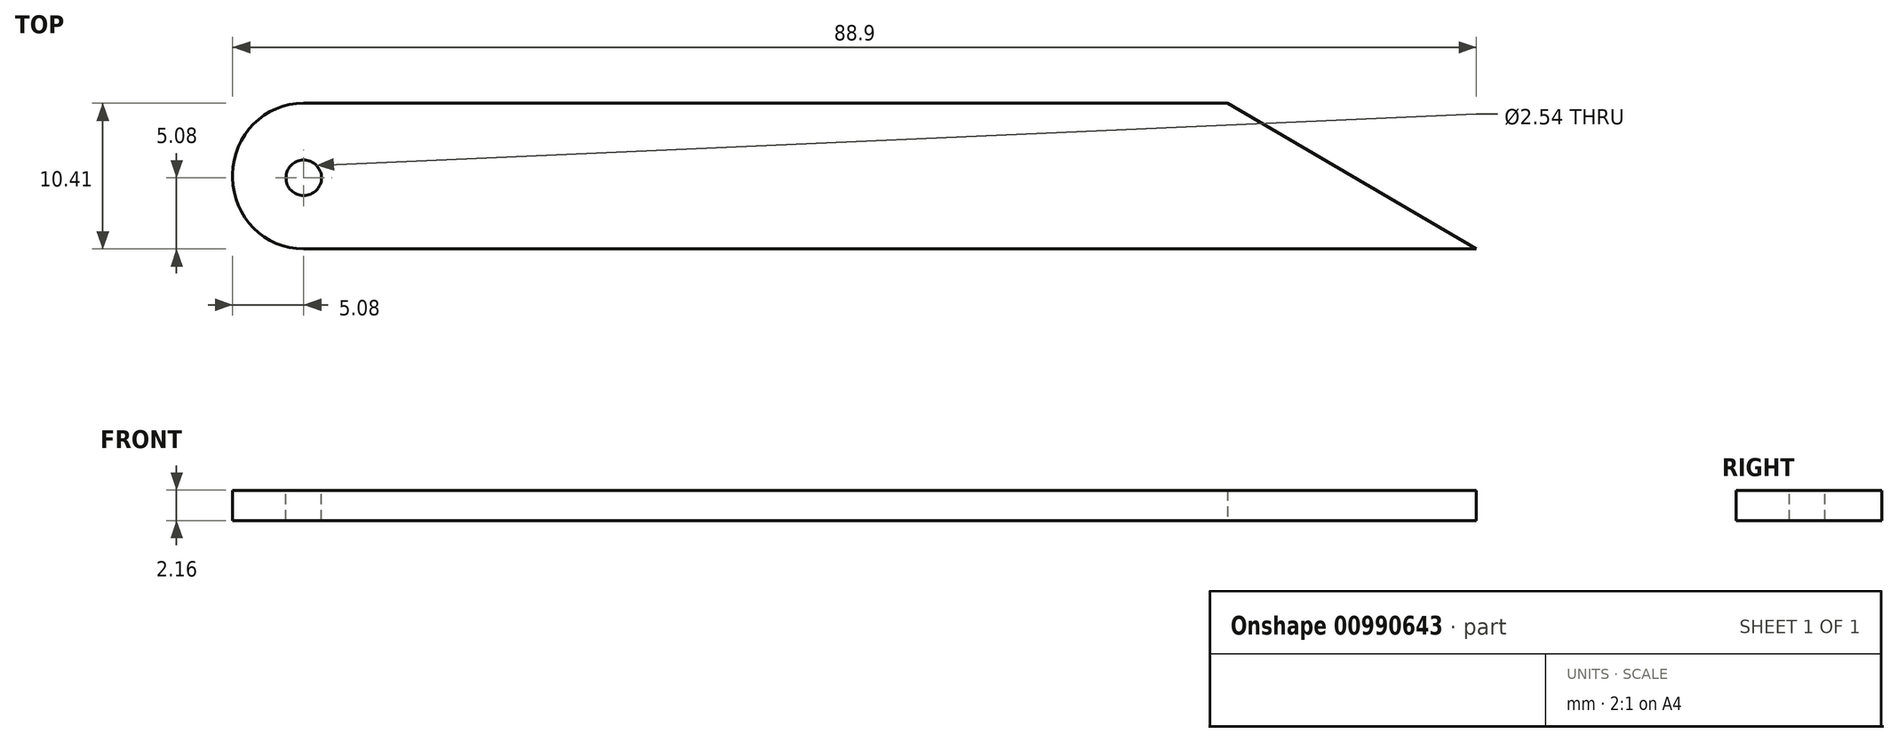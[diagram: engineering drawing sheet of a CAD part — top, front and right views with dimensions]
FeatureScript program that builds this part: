
annotation { "Feature Type Name" : "Feature", "Feature Type Description" : "" }
export const myFeature = defineFeature(function(context is Context, id is Id, definition is map)
    precondition{}
    {
        {
            var Q0;
            Q0=qCreatedBy(makeId("Top.planeOp"),FACE);
            var sketch = newSketch(context, id + "F0", { "sketchPlane" : qUnion([Q0])});
            skLineSegment(sketch, "E0.bottom", {"start": v(0, 0) * mm, "end": v(88.9, 0) * mm});
            skLineSegment(sketch, "E0.left", {"start": v(0, 0) * mm, "end": v(0, 10.41) * mm});
            skLineSegment(sketch, "E1", {"start": v(0, 10.41) * mm, "end": v(71.12, 10.41) * mm});
            skLineSegment(sketch, "E2", {"start": v(71.12, 10.41) * mm, "end": v(88.9, 0) * mm});
            skSolve(sketch);
        }
        {
            var Q0;
            Q0=makeQuery(id+"F0.imprint","IMPRINT",FACE,{"disambiguationData":[TD([[makeQuery(id+"F0.imprint","IMPRINT",EDGE,{"derivedFrom":sQuery(id+"F0.wireOp",EDGE,"E0.bottom")}),1.0]])]});
            extrude(context, id + "F1", {"entities" : qUnion([Q0]), "endBound" : BoundingType.SYMMETRIC, "depth" : 2.16 * mm, "offsetDistance" : 25.4 * mm});
        }
        {
            var Q0;
            Q0=makeQuery(id+"F1.opExtrude","SWEPT_EDGE",EDGE,{"disambiguationData":[OSD([sQuery(id+"F0.wireOp",EDGE,"E0.left"),sQuery(id+"F0.wireOp",EDGE,"E1")])]});
            var Q1;
            Q1=makeQuery(id+"F1.opExtrude","SWEPT_EDGE",EDGE,{"disambiguationData":[OSD([sQuery(id+"F0.wireOp",EDGE,"E0.bottom"),sQuery(id+"F0.wireOp",EDGE,"E0.left")])]});
            fillet(context, id + "F2", {"entities" : qUnion([Q0, Q1]), "radius" : 5.08 * mm, "tangentPropagation" : true, "allowEdgeOverflow" : false});
        }
        {
            var Q0;
            Q0=makeQuery(id+"F1.opExtrude","CAP_FACE",FACE,{"disambiguationData":[OSD([sQuery(id+"F0.wireOp",EDGE,"E0.bottom"),sQuery(id+"F0.wireOp",EDGE,"E0.left"),sQuery(id+"F0.wireOp",EDGE,"E1"),sQuery(id+"F0.wireOp",EDGE,"E2")])],"isStart":false});
            var sketch = newSketch(context, id + "F3", { "sketchPlane" : qUnion([Q0])});
            skCircle(sketch, "E3", {"center": v(5.08, 5.08) * mm, "radius": 1.27 * mm});
            skSolve(sketch);
        }
        {
            var Q0;
            Q0=makeQuery(id+"F3.imprint","IMPRINT",FACE,{"disambiguationData":[TD([[makeQuery(id+"F3.imprint","IMPRINT",EDGE,{"derivedFrom":sQuery(id+"F3.wireOp",EDGE,"E3")}),1.0]])]});
            extrude(context, id + "F4", {"entities" : qUnion([Q0]), "operationType" : NewBodyOperationType.REMOVE, "oppositeDirection" : true, "depth" : 25.4 * mm, "offsetDistance" : 25.4 * mm});
        }
    });
